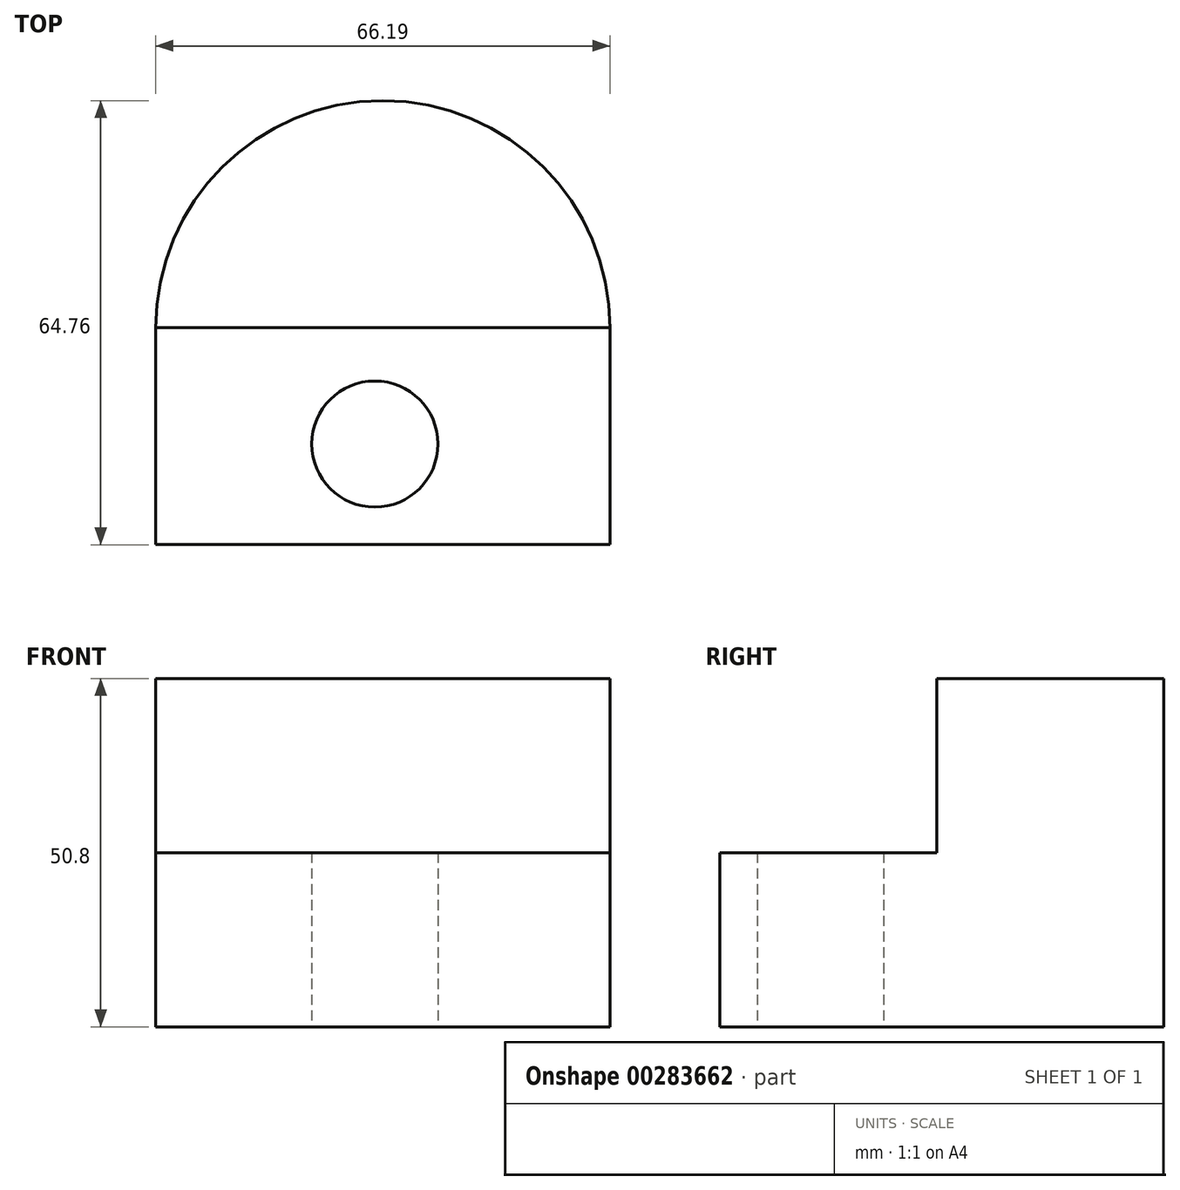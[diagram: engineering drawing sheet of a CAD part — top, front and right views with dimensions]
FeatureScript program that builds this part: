
annotation { "Feature Type Name" : "Feature", "Feature Type Description" : "" }
export const myFeature = defineFeature(function(context is Context, id is Id, definition is map)
    precondition{}
    {
        {
            var Q0;
            Q0=qCreatedBy(makeId("Top.planeOp"),FACE);
            var sketch = newSketch(context, id + "F0", { "sketchPlane" : qUnion([Q0])});
            skLineSegment(sketch, "E0.bottom", {"start": v(-20.72, 8.92) * mm, "end": v(45.47, 8.92) * mm});
            skLineSegment(sketch, "E0.top", {"start": v(-20.72, -22.74) * mm, "end": v(45.47, -22.74) * mm});
            skLineSegment(sketch, "E0.left", {"start": v(-20.72, 8.92) * mm, "end": v(-20.72, -22.74) * mm});
            skLineSegment(sketch, "E0.right", {"start": v(45.47, 8.92) * mm, "end": v(45.47, -22.74) * mm});
            skArc(sketch, "E1", {"start": v(45.47, 8.92) * mm, "mid": v(12.38, 42.02) * mm, "end": v(-20.72, 8.92) * mm});
            skCircle(sketch, "E2", {"center": v(11.22, -8.06) * mm, "radius": 9.2 * mm});
            skSolve(sketch);
        }
        {
            var Q0;
            Q0=makeQuery(id+"F0.imprint","IMPRINT",FACE,{"disambiguationData":[TD([[makeQuery(id+"F0.imprint","IMPRINT",EDGE,{"derivedFrom":sQuery(id+"F0.wireOp",EDGE,"E0.bottom")}),1.0]])]});
            extrude(context, id + "F1", {"entities" : qUnion([Q0]), "depth" : 50.8 * mm});
        }
        {
            var Q0;
            Q0 = qSketchRegion(id + "F0", true);
            extrude(context, id + "F2", {"entities" : qUnion([Q0]), "operationType" : NewBodyOperationType.ADD, "depth" : 25.4 * mm});
        }
    });
